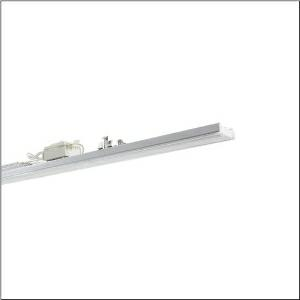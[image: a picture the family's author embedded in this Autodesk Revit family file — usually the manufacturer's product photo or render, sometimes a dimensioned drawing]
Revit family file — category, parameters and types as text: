
# Revit family: licross_11_recessed_ho_51tl12dn6d5m
name_source: partatom
category: Lighting Fixtures
units: mm (PartAtom-declared; Revit-internal decimal feet)

## family parameters
Cut with Voids When Loaded = No
Host = Face
Light Source = No
Part Type = Normal
Room Calculation Point = No
Round Connector Dimension = Use Diameter
Shared = No

## types (1)
- --- (1 x LED, 13710 lm, 76.8 W, 6500K)
    Apparent Load = 77 VA
    CIE Flux Codes = 66 91 98 100 100
    Color Rendering = 80
    Color Temperature = 6500K
    Default Elevation = 1800 mm
    Description = Licross 11 Recessed HO, luminaire insert, of sheet steel, coil coated, white, length: 1.500mm, width: 66mm, height: 67mm, LED rated luminous flux: 13.710lm, light colour: 865, SDCM (Standard Deviation of Colour Matching)MacAdam ≤ 2 SDCM (initial), control gear: DALI 2, with plug, 5-pole, with phase selection, mains connection: 220..240V, AC, 50/60Hz, rated input power: 77W, internal wiring halogen-free, primary optical cover: cover, of PMMA, light emission: direct distribution, primary light characteristic: symmetric, protection rating (complete): IP40, insulation class (complete): insulation class I (protective earthing), certification: CE, ENEC, VDE, UKCA, protection symbol: D if used in an environment without relevant dust loads with corresponding accessories, impact resistance: IK06, permissible ambient temperature for indoor applications: -25..+30°C, corresponds to IFS (International Featured Standards) requirements for safety and quality in the food industry, reducing of maximum allowable ambient temperature of 5°C with ceiling mounting, LABS conformity tested according to VDMA 24364:2018-05, The light source and the operating device comply with the requirements of the Ecodesign Regulation (EU) 2019/2020 and are replaceable in accordance with this regulation, packaging unit: 1 piece
    Height = 58 mm
    Lamp = 1 x LED
    Lamp Light Flux = 13710 lm
    Lamp Power = 76.8 W
    Lamp count = 1
    Length = 1500 mm
    Luminous efficacy = 179 lm/W
    Manufacturer = Siteco
    ModVariant = No
    Model = 51TL12DN6D5M
    Mounting Place = Ceiling
    Mounting Type = Pendant
    Number of Poles = 1
    OnlyDefault = Yes
    Power Factor = 1
    Product Name = Licross 11 Recessed HO
    Product group = luminaire insert | ceiling pendant
    ProductGroupID = 901
    Protection Class = Protection class I
    Protection Degree = IP 40
    RLX_Detail_Level = 1
    RLX_Emergency_Light_Flux = 0 lm
    RLX_Emergency_Type = 0
    RLX_Emergency_Type_DB = No
    RlxData = <blob elided: 24885 chars, md5=f8361bf7>
    Socket = socket
    Standby Power = 0 W
    System Light Flux = 13710 lm
    System Power = 77 W
    Type Comments = factory setting: luminous flux: 100 % | dim-lin: 254 | 522 mA
    Type Image = l_1296930.jpg
    URL = http://relux.com
    VarID = @adj_075341
    Voltage = 0 V
    Weight = 0.00 kg
    Width = 66 mm

## geometry (parser evidence)
native form markers: Blend x4, Sweep x10
no freeform markers — native parametric forms only
